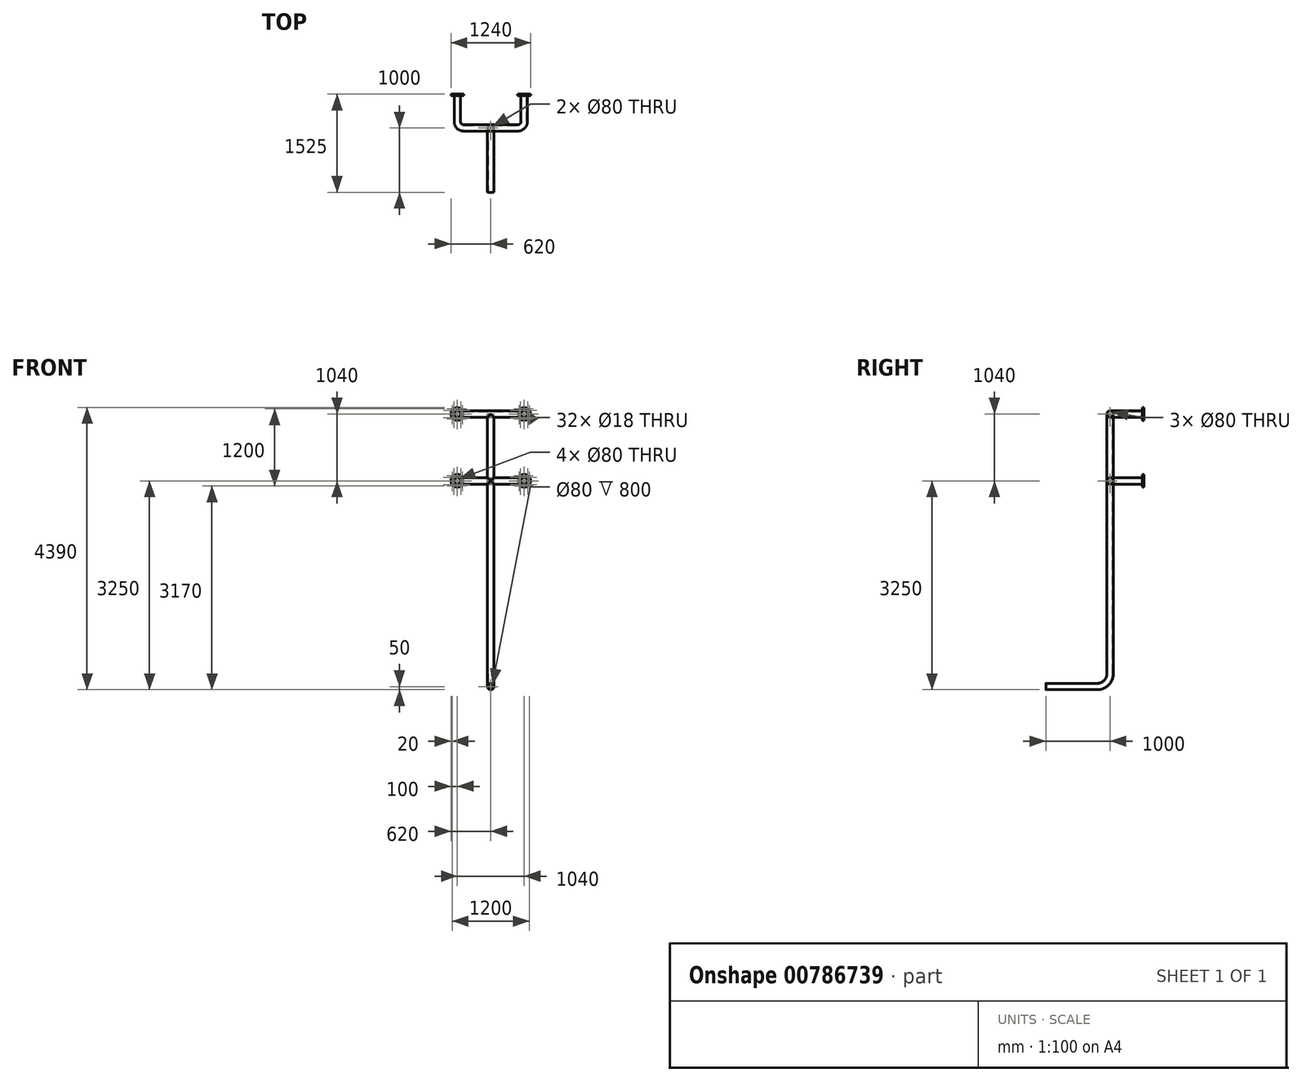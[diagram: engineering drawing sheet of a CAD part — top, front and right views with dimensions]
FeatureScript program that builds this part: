
annotation { "Feature Type Name" : "Feature", "Feature Type Description" : "" }
export const myFeature = defineFeature(function(context is Context, id is Id, definition is map)
    precondition{}
    {
        {
            var Q0;
            Q0=qCreatedBy(makeId("Front.planeOp"),FACE);
            var sketch = newSketch(context, id + "F0", { "sketchPlane" : qUnion([Q0])});
            skCircle(sketch, "E0", {"center": v(-520, 0) * mm, "radius": 40 * mm});
            skCircle(sketch, "E1", {"center": v(-520, 0) * mm, "radius": 100 * mm});
            skCircle(sketch, "E2", {"center": v(-520, 80) * mm, "radius": 9 * mm});
            skCircle(sketch, "E3.1.0", {"center": v(-576.57, 56.57) * mm, "radius": 9 * mm});
            skCircle(sketch, "E3.2.0", {"center": v(-600, 0) * mm, "radius": 9 * mm});
            skCircle(sketch, "E3.3.0", {"center": v(-576.57, -56.57) * mm, "radius": 9 * mm});
            skCircle(sketch, "E3.4.0", {"center": v(-520, -80) * mm, "radius": 9 * mm});
            skCircle(sketch, "E3.5.0", {"center": v(-463.43, -56.57) * mm, "radius": 9 * mm});
            skCircle(sketch, "E3.6.0", {"center": v(-440, 0) * mm, "radius": 9 * mm});
            skCircle(sketch, "E3.7.0", {"center": v(-463.43, 56.57) * mm, "radius": 9 * mm});
            skCircle(sketch, "E4.0.1.0", {"center": v(-520, 1040) * mm, "radius": 40 * mm});
            skCircle(sketch, "E4.0.1.1", {"center": v(-520, 1040) * mm, "radius": 100 * mm});
            skPoint(sketch, "E4.0.1.2", {"position": v(-520, 1040) * mm});
            skCircle(sketch, "E4.0.1.3", {"center": v(-576.57, 1096.57) * mm, "radius": 9 * mm});
            skCircle(sketch, "E4.0.1.4", {"center": v(-600, 1040) * mm, "radius": 9 * mm});
            skCircle(sketch, "E4.0.1.5", {"center": v(-576.57, 983.43) * mm, "radius": 9 * mm});
            skCircle(sketch, "E4.0.1.6", {"center": v(-520, 960) * mm, "radius": 9 * mm});
            skCircle(sketch, "E4.0.1.7", {"center": v(-463.43, 983.43) * mm, "radius": 9 * mm});
            skCircle(sketch, "E4.0.1.8", {"center": v(-440, 1040) * mm, "radius": 9 * mm});
            skCircle(sketch, "E4.0.1.9", {"center": v(-463.43, 1096.57) * mm, "radius": 9 * mm});
            skCircle(sketch, "E4.0.1.10", {"center": v(-520, 1120) * mm, "radius": 9 * mm});
            skCircle(sketch, "E4.1.0.0", {"center": v(520, 0) * mm, "radius": 40 * mm});
            skCircle(sketch, "E4.1.0.1", {"center": v(520, 0) * mm, "radius": 100 * mm});
            skPoint(sketch, "E4.1.0.2", {"position": v(520, 0) * mm});
            skCircle(sketch, "E4.1.0.3", {"center": v(463.43, 56.57) * mm, "radius": 9 * mm});
            skCircle(sketch, "E4.1.0.4", {"center": v(440, 0) * mm, "radius": 9 * mm});
            skCircle(sketch, "E4.1.0.5", {"center": v(463.43, -56.57) * mm, "radius": 9 * mm});
            skCircle(sketch, "E4.1.0.6", {"center": v(520, -80) * mm, "radius": 9 * mm});
            skCircle(sketch, "E4.1.0.7", {"center": v(576.57, -56.57) * mm, "radius": 9 * mm});
            skCircle(sketch, "E4.1.0.8", {"center": v(600, 0) * mm, "radius": 9 * mm});
            skCircle(sketch, "E4.1.0.9", {"center": v(576.57, 56.57) * mm, "radius": 9 * mm});
            skCircle(sketch, "E4.1.0.10", {"center": v(520, 80) * mm, "radius": 9 * mm});
            skCircle(sketch, "E4.1.1.0", {"center": v(520, 1040) * mm, "radius": 40 * mm});
            skCircle(sketch, "E4.1.1.1", {"center": v(520, 1040) * mm, "radius": 100 * mm});
            skPoint(sketch, "E4.1.1.2", {"position": v(520, 1040) * mm});
            skCircle(sketch, "E4.1.1.3", {"center": v(463.43, 1096.57) * mm, "radius": 9 * mm});
            skCircle(sketch, "E4.1.1.4", {"center": v(440, 1040) * mm, "radius": 9 * mm});
            skCircle(sketch, "E4.1.1.5", {"center": v(463.43, 983.43) * mm, "radius": 9 * mm});
            skCircle(sketch, "E4.1.1.6", {"center": v(520, 960) * mm, "radius": 9 * mm});
            skCircle(sketch, "E4.1.1.7", {"center": v(576.57, 983.43) * mm, "radius": 9 * mm});
            skCircle(sketch, "E4.1.1.8", {"center": v(600, 1040) * mm, "radius": 9 * mm});
            skCircle(sketch, "E4.1.1.9", {"center": v(576.57, 1096.57) * mm, "radius": 9 * mm});
            skCircle(sketch, "E4.1.1.10", {"center": v(520, 1120) * mm, "radius": 9 * mm});
            skLineSegment(sketch, "E4.direction1", {"start": v(-576.57, -56.57) * mm, "end": v(463.43, -56.57) * mm, "construction": true});
            skLineSegment(sketch, "E4.direction2", {"start": v(-576.57, -56.57) * mm, "end": v(-576.57, 983.43) * mm, "construction": true});
            skSolve(sketch);
        }
        {
            var Q0;
            Q0=qSketchRegion(id+"F0",true);
            extrude(context, id + "F1", {"entities" : qUnion([Q0]), "depth" : 25 * mm, "offsetDistance" : 25 * mm});
        }
        {
            var Q0;
            Q0=makeQuery(id+"F1.opExtrude","CAP_FACE",FACE,{"disambiguationData":[OSD([sQuery(id+"F0.wireOp",EDGE,"E0"),sQuery(id+"F0.wireOp",EDGE,"E1"),sQuery(id+"F0.wireOp",EDGE,"E2"),sQuery(id+"F0.wireOp",EDGE,"E3.1.0"),sQuery(id+"F0.wireOp",EDGE,"E3.2.0"),sQuery(id+"F0.wireOp",EDGE,"E3.3.0"),sQuery(id+"F0.wireOp",EDGE,"E3.4.0"),sQuery(id+"F0.wireOp",EDGE,"E3.5.0"),sQuery(id+"F0.wireOp",EDGE,"E3.6.0"),sQuery(id+"F0.wireOp",EDGE,"E3.7.0")])],"isStart":false});
            var sketch = newSketch(context, id + "F2", { "sketchPlane" : qUnion([Q0])});
            skCircle(sketch, "E5", {"center": v(-520, 0) * mm, "radius": 50 * mm});
            skCircle(sketch, "E6.0.1.0", {"center": v(-520, 1040) * mm, "radius": 50 * mm});
            skCircle(sketch, "E6.1.0.0", {"center": v(520, 0) * mm, "radius": 50 * mm});
            skCircle(sketch, "E6.1.1.0", {"center": v(520, 1040) * mm, "radius": 50 * mm});
            skLineSegment(sketch, "E6.direction1", {"start": v(-520, 0) * mm, "end": v(520, 0) * mm, "construction": true});
            skLineSegment(sketch, "E6.direction2", {"start": v(-520, 0) * mm, "end": v(-520, 1040) * mm, "construction": true});
            skCircle(sketch, "E7", {"center": v(-520, 0) * mm, "radius": 40 * mm});
            skCircle(sketch, "E8.0.1.0", {"center": v(-520, 1040) * mm, "radius": 40 * mm});
            skCircle(sketch, "E8.1.0.0", {"center": v(520, 0) * mm, "radius": 40 * mm});
            skCircle(sketch, "E8.1.1.0", {"center": v(520, 1040) * mm, "radius": 40 * mm});
            skSolve(sketch);
        }
        {
            var Q0;
            Q0=qCreatedBy(makeId("Top.planeOp"),FACE);
            var sketch = newSketch(context, id + "F3", { "sketchPlane" : qUnion([Q0])});
            skPoint(sketch, "E9.0", {"position": v(-520, -25) * mm});
            skPoint(sketch, "E10.0", {"position": v(520, -25) * mm});
            skLineSegment(sketch, "E11", {"start": v(-520, -25) * mm, "end": v(-520, -425) * mm});
            skLineSegment(sketch, "E12", {"start": v(-420, -525) * mm, "end": v(420, -525) * mm});
            skLineSegment(sketch, "E13", {"start": v(520, -425) * mm, "end": v(520, -25) * mm});
            skPoint(sketch, "E14.visualSharp", {"position": v(-520, -525) * mm});
            skArc(sketch, "E14.filletArc", {"start": v(-520, -425) * mm, "mid": v(-490.71, -495.71) * mm, "end": v(-420, -525) * mm});
            skPoint(sketch, "E15.visualSharp", {"position": v(520, -525) * mm});
            skArc(sketch, "E15.filletArc", {"start": v(420, -525) * mm, "mid": v(490.71, -495.71) * mm, "end": v(520, -425) * mm});
            skSolve(sketch);
        }
        {
            var Q0;
            Q0=qCreatedBy(makeId("Top.planeOp"),FACE);
            cPlane(context, id + "F4", {"entities" : qUnion([Q0]), "cplaneType" : CPlaneType.OFFSET, "offset" : 1040 * mm, "width" : 150 * mm, "height" : 150 * mm});
        }
        {
            var Q0;
            Q0=qCreatedBy(id+"F4.planeOp",FACE);
            var sketch = newSketch(context, id + "F5", { "sketchPlane" : qUnion([Q0])});
            skPoint(sketch, "E16.0", {"position": v(-520, -25) * mm});
            skPoint(sketch, "E17.0", {"position": v(520, -25) * mm});
            skLineSegment(sketch, "E18", {"start": v(-520, -25) * mm, "end": v(-520, -425) * mm});
            skLineSegment(sketch, "E19", {"start": v(-420, -525) * mm, "end": v(420, -525) * mm});
            skLineSegment(sketch, "E20", {"start": v(520, -425) * mm, "end": v(520, -25) * mm});
            skPoint(sketch, "E21.visualSharp", {"position": v(-520, -525) * mm});
            skArc(sketch, "E21.filletArc", {"start": v(-520, -425) * mm, "mid": v(-490.71, -495.71) * mm, "end": v(-420, -525) * mm});
            skPoint(sketch, "E22.visualSharp", {"position": v(520, -525) * mm});
            skArc(sketch, "E22.filletArc", {"start": v(420, -525) * mm, "mid": v(490.71, -495.71) * mm, "end": v(520, -425) * mm});
            skSolve(sketch);
        }
        {
            var Q0;
            Q0=qCreatedBy(makeId("Front.planeOp"),FACE);
            cPlane(context, id + "F6", {"entities" : qUnion([Q0]), "cplaneType" : CPlaneType.OFFSET, "offset" : 525 * mm, "width" : 150 * mm, "height" : 150 * mm});
        }
        {
            var Q0;
            Q0=qCreatedBy(id+"F6.planeOp",FACE);
            var sketch = newSketch(context, id + "F7", { "sketchPlane" : qUnion([Q0])});
            skLineSegment(sketch, "E23.0", {"start": v(-420, 1040) * mm, "end": v(420, 1040) * mm});
            skLineSegment(sketch, "E24.0", {"start": v(-420, 0) * mm, "end": v(420, 0) * mm});
            skLineSegment(sketch, "E25", {"start": v(0, 1040) * mm, "end": v(0, 0) * mm});
            skLineSegment(sketch, "E26", {"start": v(0, 0) * mm, "end": v(0, -200) * mm});
            skLineSegment(sketch, "E27", {"start": v(0, -200) * mm, "end": v(0, -3200) * mm});
            skSolve(sketch);
        }
        {
            var Q0;
            Q0=makeQuery(id+"F2.imprint","IMPRINT",FACE,{"disambiguationData":[TD([[makeQuery(id+"F2.imprint","IMPRINT",EDGE,{"derivedFrom":sQuery(id+"F2.wireOp",EDGE,"E6.0.1.0")}),1.0]])]});
            var Q1;
            Q1=sQuery(id+"F5.wireOp",EDGE,"E18");
            var Q2;
            Q2=sQuery(id+"F5.wireOp",EDGE,"E21.filletArc");
            var Q3;
            Q3=sQuery(id+"F7.wireOp",EDGE,"E23.0");
            var Q4;
            Q4=sQuery(id+"F5.wireOp",EDGE,"E22.filletArc");
            var Q5;
            Q5=sQuery(id+"F5.wireOp",EDGE,"E20");
            sweep(context, id + "F8", {"operationType" : NewBodyOperationType.ADD, "profiles" : qUnion([Q0]), "path" : qUnion([Q1, Q2, Q3, Q4, Q5])});
        }
        {
            var Q0;
            Q0=makeQuery(id+"F2.imprint","IMPRINT",FACE,{"disambiguationData":[TD([[makeQuery(id+"F2.imprint","IMPRINT",EDGE,{"derivedFrom":sQuery(id+"F2.wireOp",EDGE,"E5")}),1.0]])]});
            var Q1;
            Q1=sQuery(id+"F3.wireOp",EDGE,"E11");
            var Q2;
            Q2=sQuery(id+"F3.wireOp",EDGE,"E14.filletArc");
            var Q3;
            Q3=sQuery(id+"F3.wireOp",EDGE,"E12");
            var Q4;
            Q4=sQuery(id+"F3.wireOp",EDGE,"E15.filletArc");
            var Q5;
            Q5=sQuery(id+"F3.wireOp",EDGE,"E13");
            sweep(context, id + "F9", {"operationType" : NewBodyOperationType.ADD, "profiles" : qUnion([Q0]), "path" : qUnion([Q1, Q2, Q3, Q4, Q5])});
        }
        {
            var Q0;
            Q0=qCreatedBy(makeId("Top.planeOp"),FACE);
            cPlane(context, id + "F10", {"entities" : qUnion([Q0]), "cplaneType" : CPlaneType.OFFSET, "offset" : 200 * mm, "oppositeDirection" : true, "width" : 150 * mm, "height" : 150 * mm});
        }
        {
            var Q0;
            Q0=qCreatedBy(id+"F10.planeOp",FACE);
            var sketch = newSketch(context, id + "F11", { "sketchPlane" : qUnion([Q0])});
            skCircle(sketch, "E28", {"center": v(0, -525) * mm, "radius": 50 * mm});
            skCircle(sketch, "E29", {"center": v(0, -525) * mm, "radius": 40 * mm});
            skSolve(sketch);
        }
        {
            var Q0;
            Q0=makeQuery(id+"F11.imprint","IMPRINT",FACE,{"disambiguationData":[TD([[makeQuery(id+"F11.imprint","IMPRINT",EDGE,{"derivedFrom":sQuery(id+"F11.wireOp",EDGE,"E28")}),1.0]])]});
            var Q1;
            Q1=sQuery(id+"F7.wireOp",EDGE,"E26");
            var Q2;
            Q2=sQuery(id+"F7.wireOp",EDGE,"E25");
            sweep(context, id + "F12", {"operationType" : NewBodyOperationType.ADD, "profiles" : qUnion([Q0]), "path" : qUnion([Q1, Q2])});
        }
        {
            var Q0;
            Q0=qCreatedBy(makeId("Right.planeOp"),FACE);
            var sketch = newSketch(context, id + "F13", { "sketchPlane" : qUnion([Q0])});
            skLineSegment(sketch, "E30.0", {"start": v(-525, -200) * mm, "end": v(-525, -3000) * mm});
            skLineSegment(sketch, "E31", {"start": v(-725, -3200) * mm, "end": v(-1525, -3200) * mm});
            skPoint(sketch, "E32.visualSharp", {"position": v(-525, -3200) * mm});
            skArc(sketch, "E32.filletArc", {"start": v(-725, -3200) * mm, "mid": v(-583.58, -3141.42) * mm, "end": v(-525, -3000) * mm});
            skSolve(sketch);
        }
        {
            var Q0;
            Q0=makeQuery(id+"F12.opSweep","CAP_FACE",FACE,{"disambiguationData":[OSD([sQuery(id+"F7.wireOp",VERTEX,"E26.end"),sQuery(id+"F11.wireOp",EDGE,"E28"),sQuery(id+"F11.wireOp",EDGE,"E29")])],"isStart":true});
            var Q1;
            Q1=sQuery(id+"F13.wireOp",EDGE,"E30.0");
            var Q2;
            Q2=sQuery(id+"F13.wireOp",EDGE,"E32.filletArc");
            var Q3;
            Q3=sQuery(id+"F13.wireOp",EDGE,"E31");
            sweep(context, id + "F14", {"operationType" : NewBodyOperationType.ADD, "profiles" : qUnion([Q0]), "path" : qUnion([Q1, Q2, Q3])});
        }
    });
